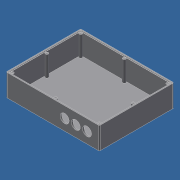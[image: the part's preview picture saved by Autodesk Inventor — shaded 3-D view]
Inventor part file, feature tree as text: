
AUTODESK INVENTOR PART (.ipt)
format: ipt  version: 2015 SP2 (Build 190223200, 223)  size: 223,232 bytes
history: native  units: mm (DEFAULTED — no unit token found)
features: other x8, sketch x8, extrude x7, fillet x1, hole x1
bodies: Solide1 (feature_tree)
feature tree (25):
  other  "Origine"
  extrude  "Extrusion1"  Depth=250.0mm
  extrude  "Extrusion2"  Depth=200.0mm
  extrude  "Extrusion3"  Depth=59.0mm TaperAngle=0.0deg
  fillet  "Congé1"  Radius=4.3mm
  extrude  "Extrusion4"  Depth=4.3mm
  extrude  "Extrusion5"  Depth=57.0mm TaperAngle=0.0deg
  extrude  "Extrusion7"  Depth=3.3mm
  hole  "Perçage1"  [1 undecoded]
  extrude  "Extrusion6"  Depth=2.0mm TaperAngle=0.0deg
  other  "Plan YZ"
  other  "Plan XZ"
  other  "Plan XY"
  other  "Axe X"
  other  "Axe Y"
  other  "Axe Z"
  other  "Point de centre"
  sketch  "Esquisse1"
  sketch  "Esquisse6"
  sketch  "Esquisse7"
  sketch  "Esquisse9"
  sketch  "Esquisse10"
  sketch  "Esquisse12"
  sketch  "Esquisse13"
  sketch  "Esquisse14"
note: 1 required parameter value undecoded (feature->parameter linkage not recoverable at this tier; creation-order binding heuristic only, values carry confidence <= 0.55)
